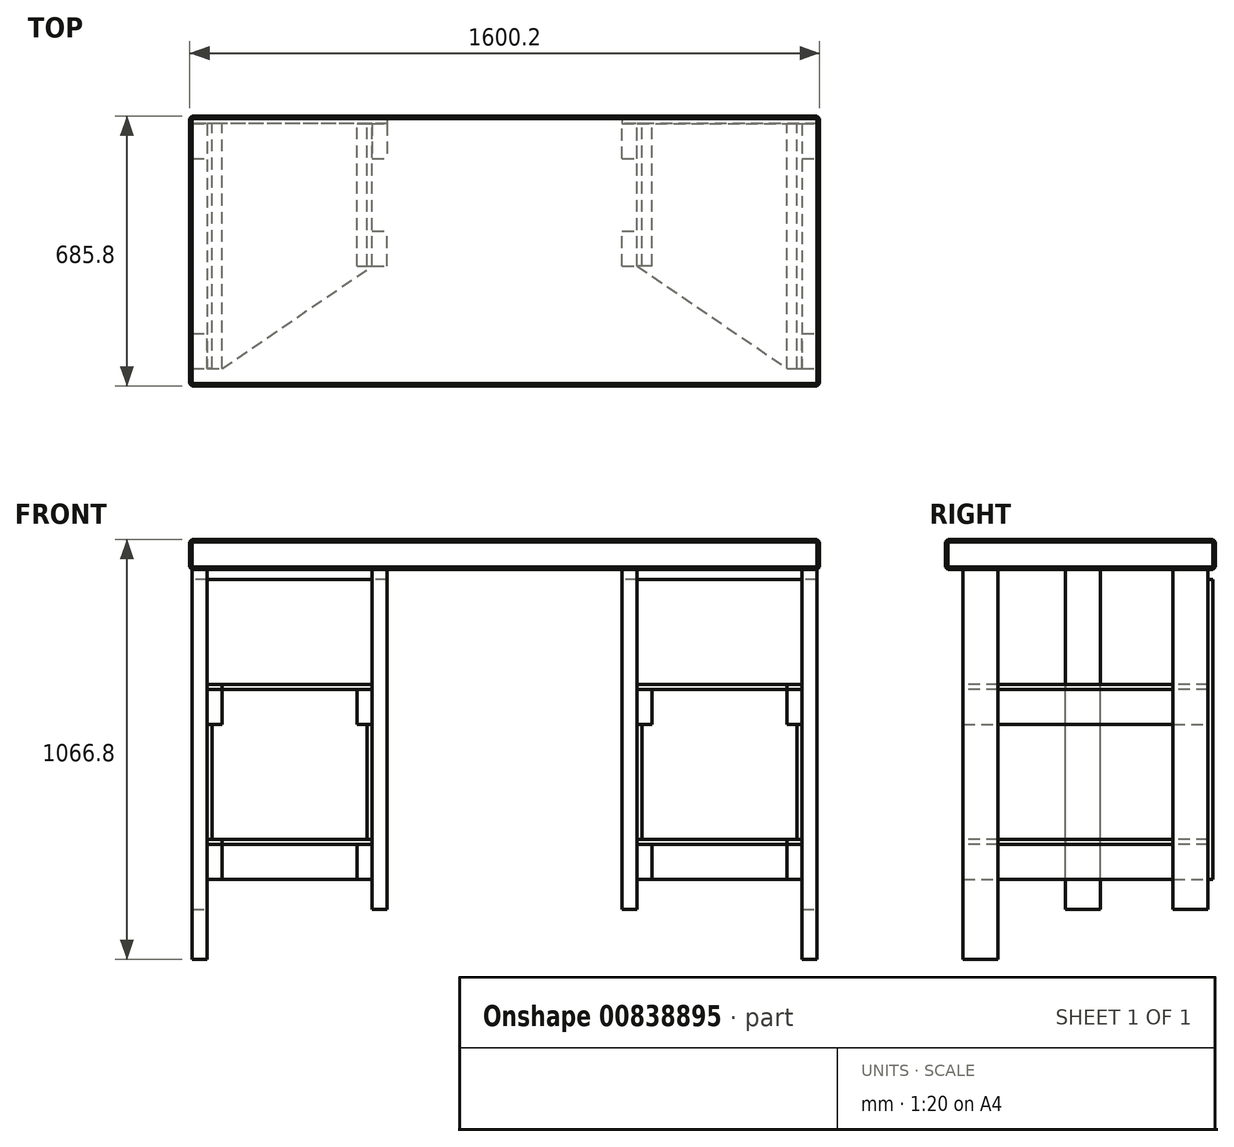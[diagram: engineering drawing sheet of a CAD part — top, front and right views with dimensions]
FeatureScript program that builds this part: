
annotation { "Feature Type Name" : "Feature", "Feature Type Description" : "" }
export const myFeature = defineFeature(function(context is Context, id is Id, definition is map)
    precondition{}
    {
        {
            var Q0;
            Q0=qCreatedBy(makeId("Top.planeOp"),FACE);
            var sketch = newSketch(context, id + "F0", { "sketchPlane" : qUnion([Q0])});
            skLineSegment(sketch, "E0.bottom", {"start": v(-438.15, -364.5) * mm, "end": v(1162.05, -364.5) * mm});
            skLineSegment(sketch, "E0.top", {"start": v(-438.15, 321.3) * mm, "end": v(1162.05, 321.3) * mm});
            skLineSegment(sketch, "E0.left", {"start": v(-438.15, -364.5) * mm, "end": v(-438.15, 321.3) * mm});
            skLineSegment(sketch, "E0.right", {"start": v(1162.05, -364.5) * mm, "end": v(1162.05, 321.3) * mm});
            skSolve(sketch);
        }
        {
            var Q0;
            Q0 = qSketchRegion(id + "F0", true);
            extrude(context, id + "F1", {"entities" : qUnion([Q0]), "depth" : 76.2 * mm, "offsetDistance" : 25 * mm});
        }
        {
            var Q0;
            Q0=makeQuery(id+"F1.opExtrude","CAP_EDGE",EDGE,{"disambiguationData":[OSD([sQuery(id+"F0.wireOp",EDGE,"E0.left")])],"isStart":false});
            var Q1;
            Q1=makeQuery(id+"F1.opExtrude","CAP_EDGE",EDGE,{"disambiguationData":[OSD([sQuery(id+"F0.wireOp",EDGE,"E0.bottom")])],"isStart":false});
            var Q2;
            Q2=makeQuery(id+"F1.opExtrude","CAP_EDGE",EDGE,{"disambiguationData":[OSD([sQuery(id+"F0.wireOp",EDGE,"E0.bottom")])],"isStart":true});
            var Q3;
            Q3=makeQuery(id+"F1.opExtrude","SWEPT_EDGE",EDGE,{"disambiguationData":[OSD([sQuery(id+"F0.wireOp",EDGE,"E0.bottom"),sQuery(id+"F0.wireOp",EDGE,"E0.left")])]});
            var Q4;
            Q4=makeQuery(id+"F1.opExtrude","SWEPT_EDGE",EDGE,{"disambiguationData":[OSD([sQuery(id+"F0.wireOp",EDGE,"E0.bottom"),sQuery(id+"F0.wireOp",EDGE,"E0.right")])]});
            var Q5;
            Q5=makeQuery(id+"F1.opExtrude","CAP_EDGE",EDGE,{"disambiguationData":[OSD([sQuery(id+"F0.wireOp",EDGE,"E0.right")])],"isStart":false});
            var Q6;
            Q6=makeQuery(id+"F1.opExtrude","CAP_EDGE",EDGE,{"disambiguationData":[OSD([sQuery(id+"F0.wireOp",EDGE,"E0.right")])],"isStart":true});
            var Q7;
            Q7=makeQuery(id+"F1.opExtrude","SWEPT_EDGE",EDGE,{"disambiguationData":[OSD([sQuery(id+"F0.wireOp",EDGE,"E0.top"),sQuery(id+"F0.wireOp",EDGE,"E0.right")])]});
            var Q8;
            Q8=makeQuery(id+"F1.opExtrude","CAP_EDGE",EDGE,{"disambiguationData":[OSD([sQuery(id+"F0.wireOp",EDGE,"E0.top")])],"isStart":false});
            var Q9;
            Q9=makeQuery(id+"F1.opExtrude","CAP_EDGE",EDGE,{"disambiguationData":[OSD([sQuery(id+"F0.wireOp",EDGE,"E0.top")])],"isStart":true});
            var Q10;
            Q10=makeQuery(id+"F1.opExtrude","SWEPT_EDGE",EDGE,{"disambiguationData":[OSD([sQuery(id+"F0.wireOp",EDGE,"E0.top"),sQuery(id+"F0.wireOp",EDGE,"E0.left")])]});
            var Q11;
            Q11=makeQuery(id+"F1.opExtrude","CAP_EDGE",EDGE,{"disambiguationData":[OSD([sQuery(id+"F0.wireOp",EDGE,"E0.left")])],"isStart":true});
            chamfer(context, id + "F2", {"entities" : qUnion([Q0, Q1, Q2, Q3, Q4, Q5, Q6, Q7, Q8, Q9, Q10, Q11]), "width" : 6.35 * mm, "tangentPropagation" : true});
        }
        {
            var Q0;
            Q0=makeQuery(id+"F1.opExtrude","CAP_FACE",FACE,{"disambiguationData":[OSD([sQuery(id+"F0.wireOp",EDGE,"E0.bottom"),sQuery(id+"F0.wireOp",EDGE,"E0.top"),sQuery(id+"F0.wireOp",EDGE,"E0.left"),sQuery(id+"F0.wireOp",EDGE,"E0.right")])],"isStart":true});
            var sketch = newSketch(context, id + "F3", { "sketchPlane" : qUnion([Q0])});
            skLineSegment(sketch, "E1.bottom", {"start": v(-431.8, -302.24) * mm, "end": v(-393.7, -302.24) * mm});
            skLineSegment(sketch, "E1.top", {"start": v(-431.8, -213.34) * mm, "end": v(-393.7, -213.34) * mm});
            skLineSegment(sketch, "E1.left", {"start": v(-431.8, -302.24) * mm, "end": v(-431.8, -213.34) * mm});
            skLineSegment(sketch, "E1.right", {"start": v(-393.7, -302.24) * mm, "end": v(-393.7, -213.34) * mm});
            skLineSegment(sketch, "E2.bottom", {"start": v(-431.8, 320.06) * mm, "end": v(-393.7, 320.06) * mm});
            skLineSegment(sketch, "E2.top", {"start": v(-431.8, 231.16) * mm, "end": v(-393.7, 231.16) * mm});
            skLineSegment(sketch, "E2.left", {"start": v(-393.7, 320.06) * mm, "end": v(-393.7, 231.16) * mm});
            skLineSegment(sketch, "E2.right", {"start": v(-431.8, 320.06) * mm, "end": v(-431.8, 231.16) * mm});
            skLineSegment(sketch, "E3.bottom", {"start": v(25.4, 59.7) * mm, "end": v(63.5, 59.7) * mm});
            skLineSegment(sketch, "E3.top", {"start": v(25.4, -29.2) * mm, "end": v(63.5, -29.2) * mm});
            skLineSegment(sketch, "E3.left", {"start": v(25.4, 59.7) * mm, "end": v(25.4, -29.2) * mm});
            skLineSegment(sketch, "E3.right", {"start": v(63.5, 59.7) * mm, "end": v(63.5, -29.2) * mm});
            skLineSegment(sketch, "E4.bottom", {"start": v(25.4, -302.24) * mm, "end": v(63.5, -302.24) * mm});
            skLineSegment(sketch, "E4.top", {"start": v(25.4, -213.34) * mm, "end": v(63.5, -213.34) * mm});
            skLineSegment(sketch, "E4.left", {"start": v(25.4, -302.24) * mm, "end": v(25.4, -213.34) * mm});
            skLineSegment(sketch, "E4.right", {"start": v(63.5, -302.24) * mm, "end": v(63.5, -213.34) * mm});
            skLineSegment(sketch, "E5.bottom", {"start": v(660.4, -213.34) * mm, "end": v(698.5, -213.34) * mm});
            skLineSegment(sketch, "E5.top", {"start": v(660.4, -302.24) * mm, "end": v(698.5, -302.24) * mm});
            skLineSegment(sketch, "E5.left", {"start": v(660.4, -213.34) * mm, "end": v(660.4, -302.24) * mm});
            skLineSegment(sketch, "E5.right", {"start": v(698.5, -213.34) * mm, "end": v(698.5, -302.24) * mm});
            skLineSegment(sketch, "E6.bottom", {"start": v(660.4, 59.7) * mm, "end": v(698.5, 59.7) * mm});
            skLineSegment(sketch, "E6.top", {"start": v(660.4, -29.2) * mm, "end": v(698.5, -29.2) * mm});
            skLineSegment(sketch, "E6.left", {"start": v(698.5, 59.7) * mm, "end": v(698.5, -29.2) * mm});
            skLineSegment(sketch, "E6.right", {"start": v(660.4, 59.7) * mm, "end": v(660.4, -29.2) * mm});
            skLineSegment(sketch, "E7.top", {"start": v(1117.6, 231.16) * mm, "end": v(1155.7, 231.16) * mm});
            skLineSegment(sketch, "E7.left", {"start": v(1117.6, 320.06) * mm, "end": v(1117.6, 231.16) * mm});
            skLineSegment(sketch, "E7.right", {"start": v(1155.7, 320.06) * mm, "end": v(1155.7, 231.16) * mm});
            skLineSegment(sketch, "E8.bottom", {"start": v(1117.6, -302.24) * mm, "end": v(1155.7, -302.24) * mm});
            skLineSegment(sketch, "E8.top", {"start": v(1117.6, -213.34) * mm, "end": v(1155.7, -213.34) * mm});
            skLineSegment(sketch, "E8.left", {"start": v(1117.6, -302.24) * mm, "end": v(1117.6, -213.34) * mm});
            skLineSegment(sketch, "E8.right", {"start": v(1155.7, -302.24) * mm, "end": v(1155.7, -213.34) * mm});
            skLineSegment(sketch, "E9", {"start": v(1117.6, 320.06) * mm, "end": v(1155.7, 320.06) * mm});
            skLineSegment(sketch, "E10", {"start": v(-393.7, -213.34) * mm, "end": v(25.4, -213.34) * mm, "construction": true});
            skLineSegment(sketch, "E11", {"start": v(698.5, -213.34) * mm, "end": v(1117.6, -213.34) * mm, "construction": true});
            skSolve(sketch);
        }
        {
            var Q0;
            Q0 = qSketchRegion(id + "F3", true);
            extrude(context, id + "F4", {"entities" : qUnion([Q0]), "depth" : 990.6 * mm, "offsetDistance" : 25.4 * mm});
        }
        {
            var Q0;
            Q0=makeQuery(id+"F4.opExtrude","CAP_FACE",FACE,{"disambiguationData":[OSD([sQuery(id+"F3.wireOp",EDGE,"E1.bottom"),sQuery(id+"F3.wireOp",EDGE,"E1.top"),sQuery(id+"F3.wireOp",EDGE,"E1.left"),sQuery(id+"F3.wireOp",EDGE,"E1.right")])],"isStart":false});
            var Q1;
            Q1=makeQuery(id+"F4.opExtrude","CAP_FACE",FACE,{"disambiguationData":[OSD([sQuery(id+"F3.wireOp",EDGE,"E4.bottom"),sQuery(id+"F3.wireOp",EDGE,"E4.top"),sQuery(id+"F3.wireOp",EDGE,"E4.left"),sQuery(id+"F3.wireOp",EDGE,"E4.right")])],"isStart":false});
            var Q2;
            Q2=makeQuery(id+"F4.opExtrude","CAP_FACE",FACE,{"disambiguationData":[OSD([sQuery(id+"F3.wireOp",EDGE,"E3.bottom"),sQuery(id+"F3.wireOp",EDGE,"E3.top"),sQuery(id+"F3.wireOp",EDGE,"E3.left"),sQuery(id+"F3.wireOp",EDGE,"E3.right")])],"isStart":false});
            var Q3;
            Q3=makeQuery(id+"F4.opExtrude","CAP_FACE",FACE,{"disambiguationData":[OSD([sQuery(id+"F3.wireOp",EDGE,"E6.bottom"),sQuery(id+"F3.wireOp",EDGE,"E6.top"),sQuery(id+"F3.wireOp",EDGE,"E6.left"),sQuery(id+"F3.wireOp",EDGE,"E6.right")])],"isStart":false});
            var Q4;
            Q4=makeQuery(id+"F4.opExtrude","CAP_FACE",FACE,{"disambiguationData":[OSD([sQuery(id+"F3.wireOp",EDGE,"E5.bottom"),sQuery(id+"F3.wireOp",EDGE,"E5.top"),sQuery(id+"F3.wireOp",EDGE,"E5.left"),sQuery(id+"F3.wireOp",EDGE,"E5.right")])],"isStart":false});
            var Q5;
            Q5=makeQuery(id+"F4.opExtrude","CAP_FACE",FACE,{"disambiguationData":[OSD([sQuery(id+"F3.wireOp",EDGE,"E8.bottom"),sQuery(id+"F3.wireOp",EDGE,"E8.top"),sQuery(id+"F3.wireOp",EDGE,"E8.left"),sQuery(id+"F3.wireOp",EDGE,"E8.right")])],"isStart":false});
            extrude(context, id + "F5", {"entities" : qUnion([Q0, Q1, Q2, Q3, Q4, Q5]), "operationType" : NewBodyOperationType.REMOVE, "oppositeDirection" : true, "depth" : 127 * mm, "offsetDistance" : 25.4 * mm});
        }
        {
            var Q0;
            Q0=makeQuery(id+"F4.opExtrude","SWEPT_FACE",FACE,{"disambiguationData":[OSD([sQuery(id+"F3.wireOp",EDGE,"E2.left")])]});
            var sketch = newSketch(context, id + "F6", { "sketchPlane" : qUnion([Q0])});
            skLineSegment(sketch, "E12.bottom", {"start": v(-320.06, -393.7) * mm, "end": v(302.24, -393.7) * mm});
            skLineSegment(sketch, "E12.top", {"start": v(-320.06, -304.8) * mm, "end": v(302.24, -304.8) * mm});
            skLineSegment(sketch, "E12.left", {"start": v(-320.06, -393.7) * mm, "end": v(-320.06, -304.8) * mm});
            skLineSegment(sketch, "E12.right", {"start": v(302.24, -393.7) * mm, "end": v(302.24, -304.8) * mm});
            skLineSegment(sketch, "E13.bottom", {"start": v(-320.06, -787.4) * mm, "end": v(302.24, -787.4) * mm});
            skLineSegment(sketch, "E13.top", {"start": v(-320.06, -698.5) * mm, "end": v(302.24, -698.5) * mm});
            skLineSegment(sketch, "E13.left", {"start": v(-320.06, -787.4) * mm, "end": v(-320.06, -698.5) * mm});
            skLineSegment(sketch, "E13.right", {"start": v(302.24, -787.4) * mm, "end": v(302.24, -698.5) * mm});
            skLineSegment(sketch, "E14", {"start": v(-320.06, -304.8) * mm, "end": v(-320.06, 0) * mm, "construction": true});
            skLineSegment(sketch, "E15", {"start": v(-320.06, -393.7) * mm, "end": v(-320.06, -698.5) * mm, "construction": true});
            skSolve(sketch);
        }
        {
            var Q0;
            Q0 = qSketchRegion(id + "F6", true);
            extrude(context, id + "F7", {"entities" : qUnion([Q0]), "depth" : 38.1 * mm, "offsetDistance" : 25.4 * mm});
        }
        {
            var Q0;
            Q0=makeQuery(id+"F4.opExtrude","SWEPT_FACE",FACE,{"disambiguationData":[OSD([sQuery(id+"F3.wireOp",EDGE,"E3.left")])]});
            var sketch = newSketch(context, id + "F8", { "sketchPlane" : qUnion([Q0])});
            skLineSegment(sketch, "E16.bottom", {"start": v(59.7, -304.8) * mm, "end": v(-302.24, -304.8) * mm});
            skLineSegment(sketch, "E16.top", {"start": v(59.7, -393.7) * mm, "end": v(-302.24, -393.7) * mm});
            skLineSegment(sketch, "E16.left", {"start": v(59.7, -304.8) * mm, "end": v(59.7, -393.7) * mm});
            skLineSegment(sketch, "E16.right", {"start": v(-302.24, -304.8) * mm, "end": v(-302.24, -393.7) * mm});
            skLineSegment(sketch, "E17.bottom", {"start": v(59.7, -698.5) * mm, "end": v(-302.24, -698.5) * mm});
            skLineSegment(sketch, "E17.top", {"start": v(59.7, -787.4) * mm, "end": v(-302.24, -787.4) * mm});
            skLineSegment(sketch, "E17.left", {"start": v(59.7, -698.5) * mm, "end": v(59.7, -787.4) * mm});
            skLineSegment(sketch, "E17.right", {"start": v(-302.24, -698.5) * mm, "end": v(-302.24, -787.4) * mm});
            skSolve(sketch);
        }
        {
            var Q0;
            Q0 = qSketchRegion(id + "F8", true);
            extrude(context, id + "F9", {"entities" : qUnion([Q0]), "depth" : 38.1 * mm, "offsetDistance" : 25.4 * mm});
        }
        {
            var Q0;
            Q0=makeQuery(id+"F4.opExtrude","SWEPT_FACE",FACE,{"disambiguationData":[OSD([sQuery(id+"F3.wireOp",EDGE,"E6.left")])]});
            var sketch = newSketch(context, id + "F10", { "sketchPlane" : qUnion([Q0])});
            skLineSegment(sketch, "E18.bottom", {"start": v(-59.7, -304.8) * mm, "end": v(302.24, -304.8) * mm});
            skLineSegment(sketch, "E18.top", {"start": v(-59.7, -393.7) * mm, "end": v(302.24, -393.7) * mm});
            skLineSegment(sketch, "E18.left", {"start": v(-59.7, -304.8) * mm, "end": v(-59.7, -393.7) * mm});
            skLineSegment(sketch, "E18.right", {"start": v(302.24, -304.8) * mm, "end": v(302.24, -393.7) * mm});
            skLineSegment(sketch, "E19.bottom", {"start": v(-59.7, -698.5) * mm, "end": v(302.24, -698.5) * mm});
            skLineSegment(sketch, "E19.top", {"start": v(-59.7, -787.4) * mm, "end": v(302.24, -787.4) * mm});
            skLineSegment(sketch, "E19.left", {"start": v(-59.7, -698.5) * mm, "end": v(-59.7, -787.4) * mm});
            skLineSegment(sketch, "E19.right", {"start": v(302.24, -698.5) * mm, "end": v(302.24, -787.4) * mm});
            skSolve(sketch);
        }
        {
            var Q0;
            Q0 = qSketchRegion(id + "F10", true);
            extrude(context, id + "F11", {"entities" : qUnion([Q0]), "depth" : 38.1 * mm, "offsetDistance" : 25.4 * mm});
        }
        {
            var Q0;
            Q0=makeQuery(id+"F4.opExtrude","SWEPT_FACE",FACE,{"disambiguationData":[OSD([sQuery(id+"F3.wireOp",EDGE,"E7.left")])]});
            var sketch = newSketch(context, id + "F12", { "sketchPlane" : qUnion([Q0])});
            skLineSegment(sketch, "E20.bottom", {"start": v(320.06, -698.5) * mm, "end": v(-302.24, -698.5) * mm});
            skLineSegment(sketch, "E20.top", {"start": v(320.06, -787.4) * mm, "end": v(-302.24, -787.4) * mm});
            skLineSegment(sketch, "E20.left", {"start": v(320.06, -698.5) * mm, "end": v(320.06, -787.4) * mm});
            skLineSegment(sketch, "E20.right", {"start": v(-302.24, -698.5) * mm, "end": v(-302.24, -787.4) * mm});
            skLineSegment(sketch, "E21.bottom", {"start": v(320.06, -304.8) * mm, "end": v(-302.24, -304.8) * mm});
            skLineSegment(sketch, "E21.top", {"start": v(320.06, -393.7) * mm, "end": v(-302.24, -393.7) * mm});
            skLineSegment(sketch, "E21.left", {"start": v(320.06, -304.8) * mm, "end": v(320.06, -393.7) * mm});
            skLineSegment(sketch, "E21.right", {"start": v(-302.24, -304.8) * mm, "end": v(-302.24, -393.7) * mm});
            skSolve(sketch);
        }
        {
            var Q0;
            Q0 = qSketchRegion(id + "F12", true);
            extrude(context, id + "F13", {"entities" : qUnion([Q0]), "depth" : 38.1 * mm, "offsetDistance" : 25.4 * mm});
        }
        {
            var Q0;
            Q0=makeQuery(id+"F9.opExtrude","SWEPT_FACE",FACE,{"disambiguationData":[OSD([sQuery(id+"F8.wireOp",EDGE,"E17.bottom")])]});
            var sketch = newSketch(context, id + "F14", { "sketchPlane" : qUnion([Q0])});
            skLineSegment(sketch, "E22.bottom", {"start": v(25.4, 302.24) * mm, "end": v(-393.7, 302.24) * mm});
            skLineSegment(sketch, "E22.left", {"start": v(25.4, 302.24) * mm, "end": v(25.4, -59.7) * mm});
            skLineSegment(sketch, "E22.right", {"start": v(-393.7, 302.24) * mm, "end": v(-393.7, -320.06) * mm});
            skPoint(sketch, "E23", {"position": v(-355.6, -320.06) * mm});
            skLineSegment(sketch, "E24", {"start": v(-393.7, -320.06) * mm, "end": v(-355.6, -320.06) * mm});
            skLineSegment(sketch, "E25", {"start": v(-355.6, -320.06) * mm, "end": v(25.4, -59.7) * mm});
            skSolve(sketch);
        }
        {
            var Q0;
            Q0 = qSketchRegion(id + "F14", true);
            extrude(context, id + "F15", {"entities" : qUnion([Q0]), "depth" : 12.7 * mm, "offsetDistance" : 25.4 * mm});
        }
        {
            var Q0;
            Q0=makeQuery(id+"F9.opExtrude","SWEPT_FACE",FACE,{"disambiguationData":[OSD([sQuery(id+"F8.wireOp",EDGE,"E16.bottom")])]});
            var sketch = newSketch(context, id + "F16", { "sketchPlane" : qUnion([Q0])});
            skLineSegment(sketch, "E26.top", {"start": v(25.4, 302.24) * mm, "end": v(-393.7, 302.24) * mm});
            skLineSegment(sketch, "E26.left", {"start": v(25.4, -59.7) * mm, "end": v(25.4, 302.24) * mm});
            skLineSegment(sketch, "E26.right", {"start": v(-393.7, -320.06) * mm, "end": v(-393.7, 302.24) * mm});
            skPoint(sketch, "E27", {"position": v(-355.6, -320.06) * mm});
            skLineSegment(sketch, "E28", {"start": v(-393.7, -320.06) * mm, "end": v(-355.6, -320.06) * mm});
            skLineSegment(sketch, "E29", {"start": v(-355.6, -320.06) * mm, "end": v(25.4, -59.7) * mm});
            skSolve(sketch);
        }
        {
            var Q0;
            Q0 = qSketchRegion(id + "F16", true);
            extrude(context, id + "F17", {"entities" : qUnion([Q0]), "depth" : 12.7 * mm, "offsetDistance" : 25.4 * mm});
        }
        {
            var Q0;
            Q0=makeQuery(id+"F11.opExtrude","SWEPT_FACE",FACE,{"disambiguationData":[OSD([sQuery(id+"F10.wireOp",EDGE,"E19.bottom")])]});
            var sketch = newSketch(context, id + "F18", { "sketchPlane" : qUnion([Q0])});
            skLineSegment(sketch, "E30.bottom", {"start": v(698.5, 302.24) * mm, "end": v(1117.6, 302.24) * mm});
            skLineSegment(sketch, "E30.left", {"start": v(698.5, 302.24) * mm, "end": v(698.5, -59.7) * mm});
            skLineSegment(sketch, "E30.right", {"start": v(1117.6, 302.24) * mm, "end": v(1117.6, -320.06) * mm});
            skPoint(sketch, "E31", {"position": v(1079.5, -320.06) * mm});
            skLineSegment(sketch, "E32", {"start": v(698.5, -59.7) * mm, "end": v(1079.5, -320.06) * mm});
            skLineSegment(sketch, "E33", {"start": v(1079.5, -320.06) * mm, "end": v(1117.6, -320.06) * mm});
            skSolve(sketch);
        }
        {
            var Q0;
            Q0 = qSketchRegion(id + "F18", true);
            extrude(context, id + "F19", {"entities" : qUnion([Q0]), "depth" : 12.7 * mm, "offsetDistance" : 25.4 * mm});
        }
        {
            var Q0;
            Q0=makeQuery(id+"F11.opExtrude","SWEPT_FACE",FACE,{"disambiguationData":[OSD([sQuery(id+"F10.wireOp",EDGE,"E18.bottom")])]});
            var sketch = newSketch(context, id + "F20", { "sketchPlane" : qUnion([Q0])});
            skLineSegment(sketch, "E34.bottom", {"start": v(698.5, 302.24) * mm, "end": v(1117.6, 302.24) * mm});
            skLineSegment(sketch, "E34.left", {"start": v(698.5, 302.24) * mm, "end": v(698.5, -59.7) * mm});
            skLineSegment(sketch, "E34.right", {"start": v(1117.6, 302.24) * mm, "end": v(1117.6, -320.06) * mm});
            skPoint(sketch, "E35", {"position": v(1079.5, -320.06) * mm});
            skLineSegment(sketch, "E36", {"start": v(698.5, -59.7) * mm, "end": v(1079.5, -320.06) * mm});
            skLineSegment(sketch, "E37", {"start": v(1079.5, -320.06) * mm, "end": v(1117.6, -320.06) * mm});
            skSolve(sketch);
        }
        {
            var Q0;
            Q0 = qSketchRegion(id + "F20", true);
            extrude(context, id + "F21", {"entities" : qUnion([Q0]), "depth" : 12.7 * mm, "offsetDistance" : 25.4 * mm});
        }
        {
            var Q0;
            Q0=makeQuery(id+"F21.boolean.opBoolean","MERGE",FACE,{"derivedFrom":[makeQuery(id+"F19.boolean.opBoolean","MERGE",FACE,{"derivedFrom":[makeQuery(id+"F11.boolean.opBoolean","MERGE",FACE,{"derivedFrom":[makeQuery(id+"F4.opExtrude","SWEPT_FACE",FACE,{"disambiguationData":[OSD([sQuery(id+"F3.wireOp",EDGE,"E5.top")])]}),makeQuery(id+"F11.opExtrude","SWEPT_FACE",FACE,{"disambiguationData":[OSD([sQuery(id+"F10.wireOp",EDGE,"E18.right")])]}),makeQuery(id+"F11.opExtrude","SWEPT_FACE",FACE,{"disambiguationData":[OSD([sQuery(id+"F10.wireOp",EDGE,"E19.right")])]})]}),makeQuery(id+"F13.boolean.opBoolean","MERGE",FACE,{"derivedFrom":[makeQuery(id+"F4.opExtrude","SWEPT_FACE",FACE,{"disambiguationData":[OSD([sQuery(id+"F3.wireOp",EDGE,"E8.bottom")])]}),makeQuery(id+"F13.opExtrude","SWEPT_FACE",FACE,{"disambiguationData":[OSD([sQuery(id+"F12.wireOp",EDGE,"E20.right")])]}),makeQuery(id+"F13.opExtrude","SWEPT_FACE",FACE,{"disambiguationData":[OSD([sQuery(id+"F12.wireOp",EDGE,"E21.right")])]})]}),makeQuery(id+"F19.opExtrude","SWEPT_FACE",FACE,{"disambiguationData":[OSD([sQuery(id+"F18.wireOp",EDGE,"E30.bottom")])]})]}),makeQuery(id+"F21.opExtrude","SWEPT_FACE",FACE,{"disambiguationData":[OSD([sQuery(id+"F20.wireOp",EDGE,"E34.bottom")])]})]});
            var sketch = newSketch(context, id + "F22", { "sketchPlane" : qUnion([Q0])});
            skLineSegment(sketch, "E38.bottom", {"start": v(-1155.7, -25.4) * mm, "end": v(-660.4, -25.4) * mm});
            skLineSegment(sketch, "E38.top", {"start": v(-1155.7, -787.4) * mm, "end": v(-660.4, -787.4) * mm});
            skLineSegment(sketch, "E38.left", {"start": v(-1155.7, -25.4) * mm, "end": v(-1155.7, -787.4) * mm});
            skLineSegment(sketch, "E38.right", {"start": v(-660.4, -25.4) * mm, "end": v(-660.4, -787.4) * mm});
            skSolve(sketch);
        }
        {
            var Q0;
            Q0 = qSketchRegion(id + "F22", true);
            extrude(context, id + "F23", {"entities" : qUnion([Q0]), "depth" : 12.7 * mm, "offsetDistance" : 25.4 * mm});
        }
        {
            var Q0;
            Q0=makeQuery(id+"F17.boolean.opBoolean","MERGE",FACE,{"derivedFrom":[makeQuery(id+"F15.boolean.opBoolean","MERGE",FACE,{"derivedFrom":[makeQuery(id+"F7.boolean.opBoolean","MERGE",FACE,{"derivedFrom":[makeQuery(id+"F4.opExtrude","SWEPT_FACE",FACE,{"disambiguationData":[OSD([sQuery(id+"F3.wireOp",EDGE,"E1.bottom")])]}),makeQuery(id+"F7.opExtrude","SWEPT_FACE",FACE,{"disambiguationData":[OSD([sQuery(id+"F6.wireOp",EDGE,"E12.right")])]}),makeQuery(id+"F7.opExtrude","SWEPT_FACE",FACE,{"disambiguationData":[OSD([sQuery(id+"F6.wireOp",EDGE,"E13.right")])]})]}),makeQuery(id+"F9.boolean.opBoolean","MERGE",FACE,{"derivedFrom":[makeQuery(id+"F4.opExtrude","SWEPT_FACE",FACE,{"disambiguationData":[OSD([sQuery(id+"F3.wireOp",EDGE,"E4.bottom")])]}),makeQuery(id+"F9.opExtrude","SWEPT_FACE",FACE,{"disambiguationData":[OSD([sQuery(id+"F8.wireOp",EDGE,"E16.right")])]}),makeQuery(id+"F9.opExtrude","SWEPT_FACE",FACE,{"disambiguationData":[OSD([sQuery(id+"F8.wireOp",EDGE,"E17.right")])]})]}),makeQuery(id+"F15.opExtrude","SWEPT_FACE",FACE,{"disambiguationData":[OSD([sQuery(id+"F14.wireOp",EDGE,"E22.bottom")])]})]}),makeQuery(id+"F17.opExtrude","SWEPT_FACE",FACE,{"disambiguationData":[OSD([sQuery(id+"F16.wireOp",EDGE,"E26.top")])]})]});
            var sketch = newSketch(context, id + "F24", { "sketchPlane" : qUnion([Q0])});
            skLineSegment(sketch, "E39.bottom", {"start": v(-63.5, -25.4) * mm, "end": v(431.8, -25.4) * mm});
            skLineSegment(sketch, "E39.top", {"start": v(-63.5, -787.4) * mm, "end": v(431.8, -787.4) * mm});
            skLineSegment(sketch, "E39.left", {"start": v(-63.5, -25.4) * mm, "end": v(-63.5, -787.4) * mm});
            skLineSegment(sketch, "E39.right", {"start": v(431.8, -25.4) * mm, "end": v(431.8, -787.4) * mm});
            skSolve(sketch);
        }
        {
            var Q0;
            Q0 = qSketchRegion(id + "F24", true);
            extrude(context, id + "F25", {"entities" : qUnion([Q0]), "depth" : 12.7 * mm, "offsetDistance" : 25.4 * mm});
        }
        {
            var Q0;
            Q0=makeQuery(id+"F4.opExtrude","SWEPT_FACE",FACE,{"disambiguationData":[OSD([sQuery(id+"F3.wireOp",EDGE,"E2.left")])]});
            var sketch = newSketch(context, id + "F26", { "sketchPlane" : qUnion([Q0])});
            skLineSegment(sketch, "E40.bottom", {"start": v(-320.06, -393.7) * mm, "end": v(302.24, -393.7) * mm});
            skLineSegment(sketch, "E40.top", {"start": v(-320.06, -685.8) * mm, "end": v(302.24, -685.8) * mm});
            skLineSegment(sketch, "E40.left", {"start": v(-320.06, -393.7) * mm, "end": v(-320.06, -685.8) * mm});
            skLineSegment(sketch, "E40.right", {"start": v(302.24, -393.7) * mm, "end": v(302.24, -685.8) * mm});
            skSolve(sketch);
        }
        {
            var Q0;
            Q0 = qSketchRegion(id + "F26", true);
            extrude(context, id + "F27", {"entities" : qUnion([Q0]), "depth" : 12.7 * mm, "offsetDistance" : 25.4 * mm});
        }
        {
            var Q0;
            Q0=makeQuery(id+"F4.opExtrude","SWEPT_FACE",FACE,{"disambiguationData":[OSD([sQuery(id+"F3.wireOp",EDGE,"E3.left")])]});
            var sketch = newSketch(context, id + "F28", { "sketchPlane" : qUnion([Q0])});
            skLineSegment(sketch, "E41.bottom", {"start": v(59.7, -393.7) * mm, "end": v(-302.24, -393.7) * mm});
            skLineSegment(sketch, "E41.top", {"start": v(59.7, -685.8) * mm, "end": v(-302.24, -685.8) * mm});
            skLineSegment(sketch, "E41.left", {"start": v(59.7, -393.7) * mm, "end": v(59.7, -685.8) * mm});
            skLineSegment(sketch, "E41.right", {"start": v(-302.24, -393.7) * mm, "end": v(-302.24, -685.8) * mm});
            skSolve(sketch);
        }
        {
            var Q0;
            Q0 = qSketchRegion(id + "F28", true);
            extrude(context, id + "F29", {"entities" : qUnion([Q0]), "depth" : 12.7 * mm, "offsetDistance" : 25.4 * mm});
        }
        {
            var Q0;
            Q0=makeQuery(id+"F4.opExtrude","SWEPT_FACE",FACE,{"disambiguationData":[OSD([sQuery(id+"F3.wireOp",EDGE,"E6.left")])]});
            var sketch = newSketch(context, id + "F30", { "sketchPlane" : qUnion([Q0])});
            skLineSegment(sketch, "E42.bottom", {"start": v(-59.7, -685.8) * mm, "end": v(302.24, -685.8) * mm});
            skLineSegment(sketch, "E42.top", {"start": v(-59.7, -393.7) * mm, "end": v(302.24, -393.7) * mm});
            skLineSegment(sketch, "E42.left", {"start": v(-59.7, -685.8) * mm, "end": v(-59.7, -393.7) * mm});
            skLineSegment(sketch, "E42.right", {"start": v(302.24, -685.8) * mm, "end": v(302.24, -393.7) * mm});
            skSolve(sketch);
        }
        {
            var Q0;
            Q0 = qSketchRegion(id + "F30", true);
            extrude(context, id + "F31", {"entities" : qUnion([Q0]), "depth" : 12.7 * mm, "offsetDistance" : 25.4 * mm});
        }
        {
            var Q0;
            Q0=makeQuery(id+"F4.opExtrude","SWEPT_FACE",FACE,{"disambiguationData":[OSD([sQuery(id+"F3.wireOp",EDGE,"E7.left")])]});
            var sketch = newSketch(context, id + "F32", { "sketchPlane" : qUnion([Q0])});
            skLineSegment(sketch, "E43.bottom", {"start": v(320.06, -393.7) * mm, "end": v(-302.24, -393.7) * mm});
            skLineSegment(sketch, "E43.top", {"start": v(320.06, -685.8) * mm, "end": v(-302.24, -685.8) * mm});
            skLineSegment(sketch, "E43.left", {"start": v(320.06, -393.7) * mm, "end": v(320.06, -685.8) * mm});
            skLineSegment(sketch, "E43.right", {"start": v(-302.24, -393.7) * mm, "end": v(-302.24, -685.8) * mm});
            skSolve(sketch);
        }
        {
            var Q0;
            Q0 = qSketchRegion(id + "F32", true);
            extrude(context, id + "F33", {"entities" : qUnion([Q0]), "depth" : 12.7 * mm, "offsetDistance" : 25.4 * mm});
        }
    });
